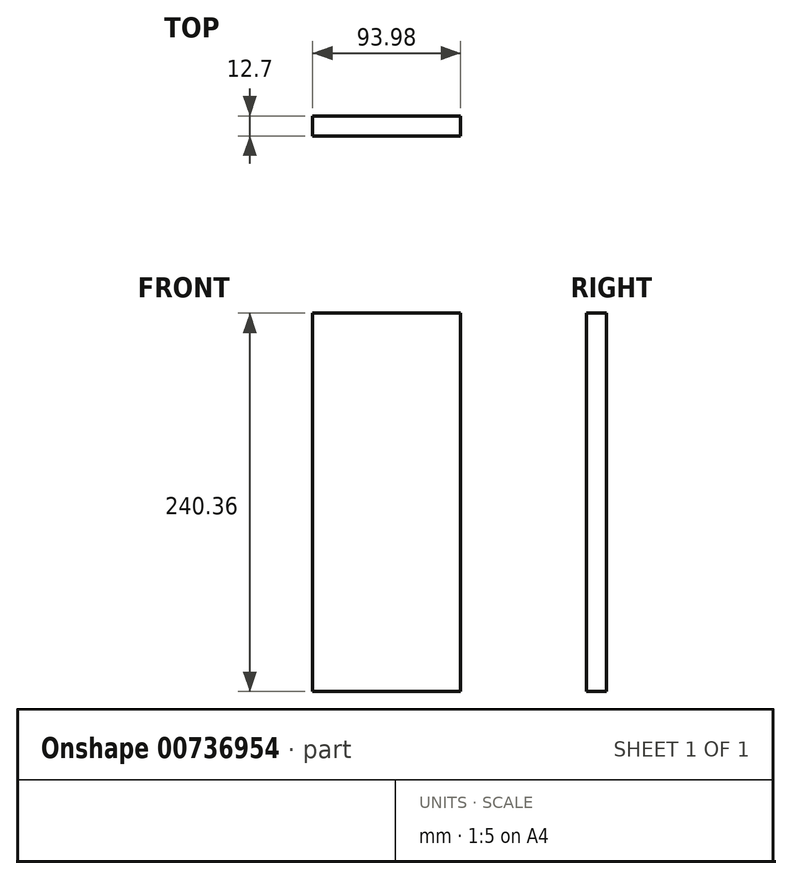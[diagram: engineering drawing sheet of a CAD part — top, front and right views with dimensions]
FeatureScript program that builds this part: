
annotation { "Feature Type Name" : "Feature", "Feature Type Description" : "" }
export const myFeature = defineFeature(function(context is Context, id is Id, definition is map)
    precondition{}
    {
        {
            var Q0;
            Q0=qCreatedBy(makeId("Front.planeOp"),FACE);
            var sketch = newSketch(context, id + "F0", { "sketchPlane" : qUnion([Q0])});
            skLineSegment(sketch, "E0.bottom", {"start": v(-46.99, 120.18) * mm, "end": v(47, 120.18) * mm});
            skLineSegment(sketch, "E0.top", {"start": v(-47, -120.18) * mm, "end": v(46.99, -120.18) * mm});
            skLineSegment(sketch, "E0.left", {"start": v(-46.99, 120.18) * mm, "end": v(-47, -120.18) * mm});
            skLineSegment(sketch, "E0.right", {"start": v(47, 120.18) * mm, "end": v(46.99, -120.18) * mm});
            skPoint(sketch, "E0.middle", {"position": v(0, 0) * mm});
            skSolve(sketch);
        }
        {
            var Q0;
            Q0=qSketchRegion(id+"F0",true);
            extrude(context, id + "F1", {"entities" : qUnion([Q0]), "depth" : 12.7 * mm, "offsetDistance" : 25.4 * mm});
        }
    });
